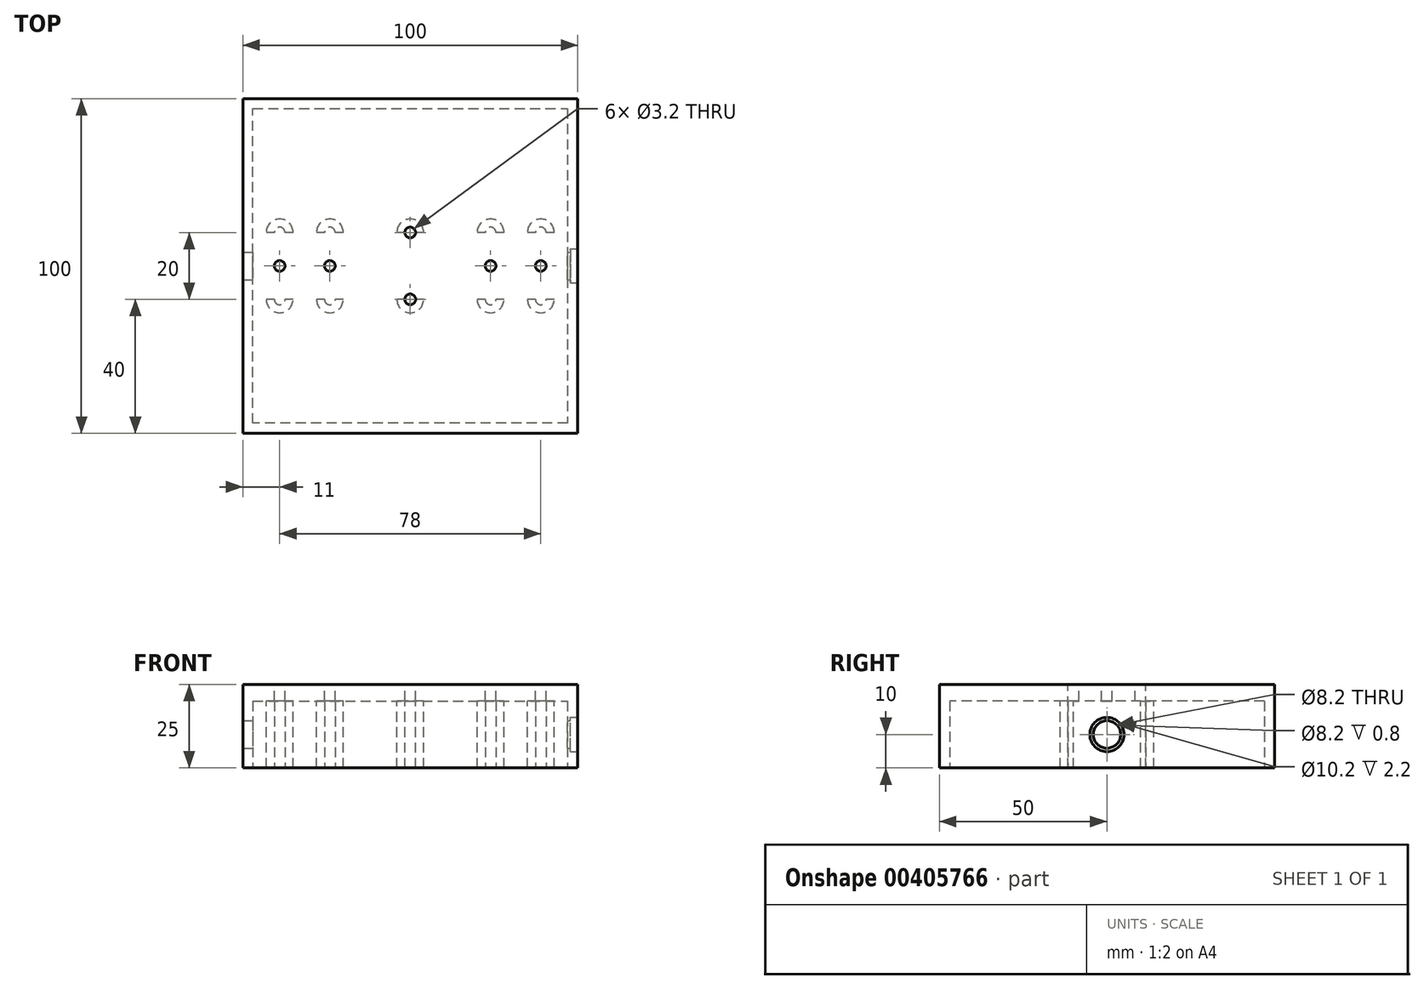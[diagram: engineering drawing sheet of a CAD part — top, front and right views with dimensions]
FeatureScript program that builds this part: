
annotation { "Feature Type Name" : "Feature", "Feature Type Description" : "" }
export const myFeature = defineFeature(function(context is Context, id is Id, definition is map)
    precondition{}
    {
        {
            var Q0;
            Q0=qCreatedBy(makeId("Top.planeOp"),FACE);
            var sketch = newSketch(context, id + "F0", { "sketchPlane" : qUnion([Q0])});
            skLineSegment(sketch, "E0.bottom", {"start": v(50, -50) * mm, "end": v(-50, -50) * mm});
            skLineSegment(sketch, "E0.top", {"start": v(50, 50) * mm, "end": v(-50, 50) * mm});
            skLineSegment(sketch, "E0.left", {"start": v(50, -50) * mm, "end": v(50, 50) * mm});
            skLineSegment(sketch, "E0.right", {"start": v(-50, -50) * mm, "end": v(-50, 50) * mm});
            skPoint(sketch, "E0.middle", {"position": v(0, 0) * mm});
            skSolve(sketch);
        }
        {
            var Q0;
            Q0=makeQuery(id+"F0.imprint","IMPRINT",FACE,{"disambiguationData":[TD([[makeQuery(id+"F0.imprint","IMPRINT",EDGE,{"derivedFrom":sQuery(id+"F0.wireOp",EDGE,"E0.bottom")}),-1.0]])]});
            extrude(context, id + "F1", {"entities" : qUnion([Q0]), "depth" : 25 * mm});
        }
        {
            var Q0;
            Q0=qCreatedBy(makeId("Top.planeOp"),FACE);
            var sketch = newSketch(context, id + "F2", { "sketchPlane" : qUnion([Q0])});
            skLineSegment(sketch, "E1.0", {"start": v(47, 47) * mm, "end": v(47, -47) * mm});
            skLineSegment(sketch, "E1.1", {"start": v(-47, 47) * mm, "end": v(47, 47) * mm});
            skLineSegment(sketch, "E1.2", {"start": v(-47, -47) * mm, "end": v(-47, 47) * mm});
            skLineSegment(sketch, "E1.3", {"start": v(47, -47) * mm, "end": v(-47, -47) * mm});
            skSolve(sketch);
        }
        {
            var Q0;
            Q0=makeQuery(id+"F2.imprint","IMPRINT",FACE,{"disambiguationData":[TD([[makeQuery(id+"F2.imprint","IMPRINT",EDGE,{"derivedFrom":sQuery(id+"F2.wireOp",EDGE,"E1.0")}),-1.0]])]});
            extrude(context, id + "F3", {"entities" : qUnion([Q0]), "operationType" : NewBodyOperationType.REMOVE, "depth" : 20 * mm});
        }
        {
            var Q0;
            Q0=makeQuery(id+"F1.opExtrude","SWEPT_FACE",FACE,{"disambiguationData":[OSD([sQuery(id+"F0.wireOp",EDGE,"E0.left")])]});
            var sketch = newSketch(context, id + "F4", { "sketchPlane" : qUnion([Q0])});
            skCircle(sketch, "E2", {"center": v(0, 10) * mm, "radius": 5 * mm});
            skSolve(sketch);
        }
        {
            var Q0;
            Q0=sQuery(id+"F4.wireOp",VERTEX,"E2.center");
            var Q1;
            Q1=makeQuery(id+"F1.opExtrude","SWEPT_BODY",BODY,{"disambiguationData":[OSD([sQuery(id+"F0.wireOp",EDGE,"E0.bottom"),sQuery(id+"F0.wireOp",EDGE,"E0.top"),sQuery(id+"F0.wireOp",EDGE,"E0.left"),sQuery(id+"F0.wireOp",EDGE,"E0.right")])]});
            hole(context, id + "F5", {"style" : HoleStyle.C_BORE, "endStyle" : HoleEndStyle.THROUGH, "holeDiameter" : 8.2 * mm, "cBoreDiameter" : 10.2 * mm, "cBoreDepth" : 2.2 * mm, "isTappedThrough" : true, "tappedDepth" : 12 * mm, "tapClearance" : 3, "startFromSketch" : true, "locations" : qUnion([Q0]), "scope" : qUnion([Q1])});
        }
        {
            var Q0;
            Q0=makeQuery(id+"F1.opExtrude","CAP_FACE",FACE,{"disambiguationData":[OSD([sQuery(id+"F0.wireOp",EDGE,"E0.bottom"),sQuery(id+"F0.wireOp",EDGE,"E0.top"),sQuery(id+"F0.wireOp",EDGE,"E0.left"),sQuery(id+"F0.wireOp",EDGE,"E0.right")])],"isStart":false});
            var sketch = newSketch(context, id + "F6", { "sketchPlane" : qUnion([Q0])});
            skLineSegment(sketch, "E3", {"start": v(0, 0) * mm, "end": v(0, -10) * mm, "construction": true});
            skCircle(sketch, "E4", {"center": v(0, -10) * mm, "radius": 4 * mm});
            skLineSegment(sketch, "E5", {"start": v(0, 0) * mm, "end": v(0, 10) * mm, "construction": true});
            skCircle(sketch, "E6", {"center": v(0, 10) * mm, "radius": 4 * mm});
            skLineSegment(sketch, "E7", {"start": v(0, 10) * mm, "end": v(-24, 10) * mm, "construction": true});
            skLineSegment(sketch, "E8", {"start": v(-24, 10) * mm, "end": v(-39, 10) * mm, "construction": true});
            skLineSegment(sketch, "E9", {"start": v(0, 10) * mm, "end": v(24, 10) * mm, "construction": true});
            skLineSegment(sketch, "E10", {"start": v(0, -10) * mm, "end": v(-24, -10) * mm, "construction": true});
            skLineSegment(sketch, "E11", {"start": v(0, -10) * mm, "end": v(24, -10) * mm, "construction": true});
            skLineSegment(sketch, "E12", {"start": v(24, -10) * mm, "end": v(39, -10) * mm, "construction": true});
            skCircle(sketch, "E13", {"center": v(-24, 10) * mm, "radius": 4 * mm});
            skCircle(sketch, "E14", {"center": v(-39, 10) * mm, "radius": 4 * mm});
            skCircle(sketch, "E15", {"center": v(24, 10) * mm, "radius": 4 * mm});
            skCircle(sketch, "E16", {"center": v(39, 10) * mm, "radius": 4 * mm});
            skCircle(sketch, "E17", {"center": v(-24, -10) * mm, "radius": 4 * mm});
            skCircle(sketch, "E18", {"center": v(24, -10) * mm, "radius": 4 * mm});
            skCircle(sketch, "E19", {"center": v(39, -10) * mm, "radius": 4 * mm});
            skLineSegment(sketch, "E20", {"start": v(-24, -10) * mm, "end": v(-39, -10) * mm, "construction": true});
            skCircle(sketch, "E21", {"center": v(-39, -10) * mm, "radius": 4 * mm});
            skLineSegment(sketch, "E22", {"start": v(24, 10) * mm, "end": v(39, 10) * mm, "construction": true});
            skSolve(sketch);
        }
        {
            var Q0;
            Q0 = qSketchRegion(id + "F6", true);
            extrude(context, id + "F7", {"entities" : qUnion([Q0]), "operationType" : NewBodyOperationType.ADD, "oppositeDirection" : true, "depth" : 25 * mm});
        }
        {
            var Q0;
            Q0=makeQuery(id+"F1.opExtrude","CAP_FACE",FACE,{"disambiguationData":[OSD([sQuery(id+"F0.wireOp",EDGE,"E0.bottom"),sQuery(id+"F0.wireOp",EDGE,"E0.top"),sQuery(id+"F0.wireOp",EDGE,"E0.left"),sQuery(id+"F0.wireOp",EDGE,"E0.right")])],"isStart":false});
            var sketch = newSketch(context, id + "F8", { "sketchPlane" : qUnion([Q0])});
            skCircle(sketch, "E23", {"center": v(39, 0) * mm, "radius": 1.5 * mm});
            skCircle(sketch, "E24", {"center": v(-24, 0) * mm, "radius": 1.5 * mm});
            skCircle(sketch, "E25", {"center": v(-39, 0) * mm, "radius": 1.5 * mm});
            skCircle(sketch, "E26", {"center": v(24, 0) * mm, "radius": 1.5 * mm});
            skCircle(sketch, "E27", {"center": v(0, 10) * mm, "radius": 1.5 * mm});
            skCircle(sketch, "E28", {"center": v(0, -10) * mm, "radius": 1.5 * mm});
            skSolve(sketch);
        }
        {
            var Q0;
            Q0=sQuery(id+"F8.wireOp",VERTEX,"E25.center");
            var Q1;
            Q1=sQuery(id+"F8.wireOp",VERTEX,"E24.center");
            var Q2;
            Q2=sQuery(id+"F8.wireOp",VERTEX,"E27.center");
            var Q3;
            Q3=sQuery(id+"F8.wireOp",VERTEX,"E26.center");
            var Q4;
            Q4=sQuery(id+"F8.wireOp",VERTEX,"E23.center");
            var Q5;
            Q5=sQuery(id+"F8.wireOp",VERTEX,"E28.center");
            var Q6;
            Q6=makeQuery(id+"F1.opExtrude","SWEPT_BODY",BODY,{"disambiguationData":[OSD([sQuery(id+"F0.wireOp",EDGE,"E0.bottom"),sQuery(id+"F0.wireOp",EDGE,"E0.top"),sQuery(id+"F0.wireOp",EDGE,"E0.left"),sQuery(id+"F0.wireOp",EDGE,"E0.right")])]});
            hole(context, id + "F9", {"style" : HoleStyle.SIMPLE, "endStyle" : HoleEndStyle.THROUGH, "holeDiameter" : 3.2 * mm, "isTappedThrough" : true, "tappedDepth" : 12 * mm, "tapClearance" : 3, "startFromSketch" : true, "locations" : qUnion([Q0, Q1, Q2, Q3, Q4, Q5]), "scope" : qUnion([Q6])});
        }
        {
            var Q0;
            Q0=qCreatedBy(makeId("Top.planeOp"),FACE);
            var sketch = newSketch(context, id + "F10", { "sketchPlane" : qUnion([Q0])});
            skLineSegment(sketch, "E29", {"start": v(0, 0) * mm, "end": v(-24, 0) * mm, "construction": true});
            skLineSegment(sketch, "E30", {"start": v(-24, 0) * mm, "end": v(-24, 10) * mm, "construction": true});
            skLineSegment(sketch, "E31", {"start": v(-24, 10) * mm, "end": v(-39, 10) * mm, "construction": true});
            skLineSegment(sketch, "E32", {"start": v(-24, 0) * mm, "end": v(-24, -10) * mm, "construction": true});
            skLineSegment(sketch, "E33", {"start": v(-24, -10) * mm, "end": v(-39, -10) * mm, "construction": true});
            skLineSegment(sketch, "E34", {"start": v(0, 0) * mm, "end": v(24, 0) * mm, "construction": true});
            skLineSegment(sketch, "E35", {"start": v(24, 0) * mm, "end": v(24, 10) * mm, "construction": true});
            skLineSegment(sketch, "E36", {"start": v(24, 10) * mm, "end": v(39, 10) * mm, "construction": true});
            skLineSegment(sketch, "E37", {"start": v(24, 0) * mm, "end": v(24, -10) * mm, "construction": true});
            skLineSegment(sketch, "E38", {"start": v(24, -10) * mm, "end": v(39, -10) * mm, "construction": true});
            skCircle(sketch, "E39", {"center": v(-39, -10) * mm, "radius": 1.6 * mm});
            skCircle(sketch, "E40", {"center": v(-24, -10) * mm, "radius": 1.6 * mm});
            skCircle(sketch, "E41", {"center": v(-24, 10) * mm, "radius": 1.6 * mm});
            skCircle(sketch, "E42", {"center": v(-39, 10) * mm, "radius": 1.6 * mm});
            skCircle(sketch, "E43", {"center": v(24, 10) * mm, "radius": 1.6 * mm});
            skCircle(sketch, "E44", {"center": v(39, 10) * mm, "radius": 1.6 * mm});
            skCircle(sketch, "E45", {"center": v(39, -10) * mm, "radius": 1.6 * mm});
            skCircle(sketch, "E46", {"center": v(24, -10) * mm, "radius": 1.6 * mm});
            skSolve(sketch);
        }
        {
            var Q0;
            Q0 = qSketchRegion(id + "F10", true);
            extrude(context, id + "F11", {"entities" : qUnion([Q0]), "operationType" : NewBodyOperationType.REMOVE, "depth" : 20 * mm});
        }
        {
            var Q0;
            Q0=qCreatedBy(makeId("Top.planeOp"),FACE);
            var sketch = newSketch(context, id + "F12", { "sketchPlane" : qUnion([Q0])});
            skLineSegment(sketch, "E47.bottom", {"start": v(47, 10) * mm, "end": v(-47, 10) * mm});
            skLineSegment(sketch, "E47.top", {"start": v(47, -10) * mm, "end": v(-47, -10) * mm});
            skLineSegment(sketch, "E47.left", {"start": v(47, 10) * mm, "end": v(47, -10) * mm});
            skLineSegment(sketch, "E47.right", {"start": v(-47, 10) * mm, "end": v(-47, -10) * mm});
            skPoint(sketch, "E47.middle", {"position": v(0, 0) * mm});
            skSolve(sketch);
        }
        {
            var Q0;
            Q0=makeQuery(id+"F12.imprint","IMPRINT",FACE,{"disambiguationData":[TD([[makeQuery(id+"F12.imprint","IMPRINT",EDGE,{"derivedFrom":sQuery(id+"F12.wireOp",EDGE,"E47.bottom")}),1.0]])]});
            extrude(context, id + "F13", {"entities" : qUnion([Q0]), "operationType" : NewBodyOperationType.REMOVE, "depth" : 20 * mm});
        }
    });
